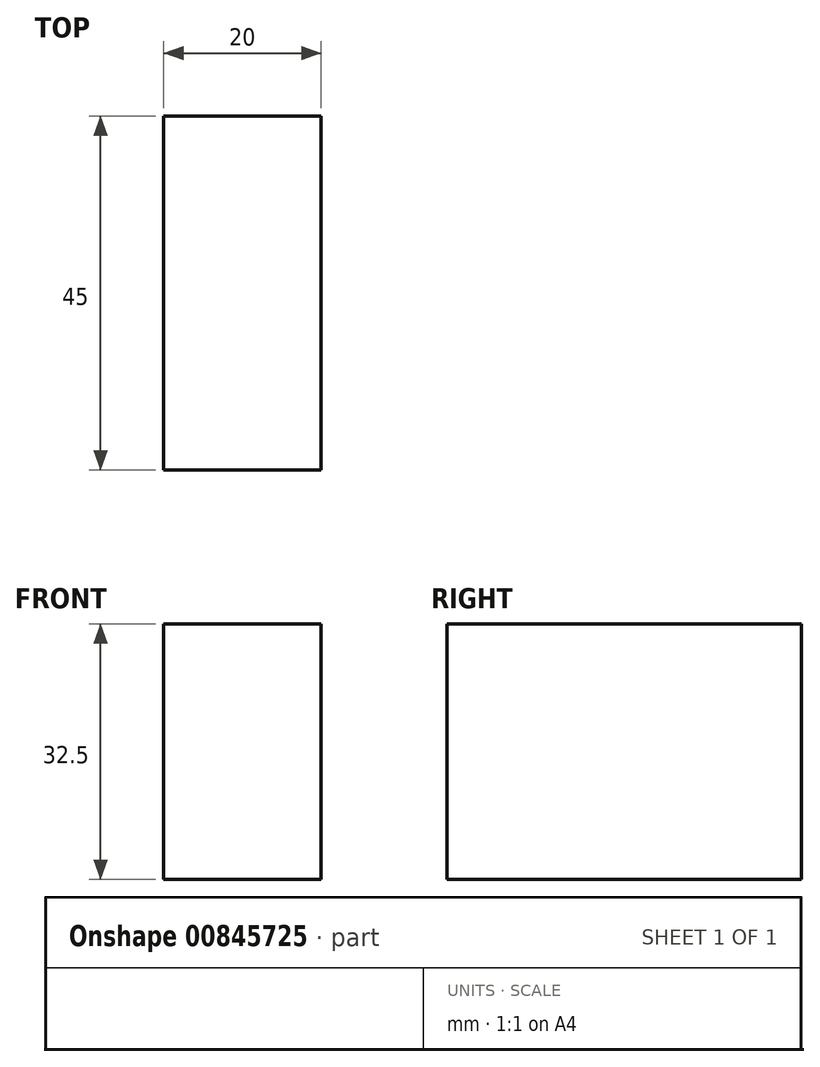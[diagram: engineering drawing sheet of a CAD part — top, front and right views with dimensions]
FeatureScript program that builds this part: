
annotation { "Feature Type Name" : "Feature", "Feature Type Description" : "" }
export const myFeature = defineFeature(function(context is Context, id is Id, definition is map)
    precondition{}
    {
        {
            var Q0;
            Q0=qCreatedBy(makeId("Right.planeOp"),FACE);
            var sketch = newSketch(context, id + "F0", { "sketchPlane" : qUnion([Q0])});
            skLineSegment(sketch, "E0.bottom", {"start": v(0, 0) * mm, "end": v(-45, 0) * mm});
            skLineSegment(sketch, "E0.top", {"start": v(0, 32.5) * mm, "end": v(-45, 32.5) * mm});
            skLineSegment(sketch, "E0.left", {"start": v(0, 0) * mm, "end": v(0, 32.5) * mm});
            skLineSegment(sketch, "E0.right", {"start": v(-45, 0) * mm, "end": v(-45, 32.5) * mm});
            skSolve(sketch);
        }
        {
            var Q0;
            Q0=makeQuery(id+"F0.imprint","IMPRINT",FACE,{"disambiguationData":[TD([[makeQuery(id+"F0.imprint","IMPRINT",EDGE,{"derivedFrom":sQuery(id+"F0.wireOp",EDGE,"E0.bottom")}),-1.0]])]});
            extrude(context, id + "F1", {"entities" : qUnion([Q0]), "depth" : 20 * mm, "offsetDistance" : 25 * mm});
        }
    });
